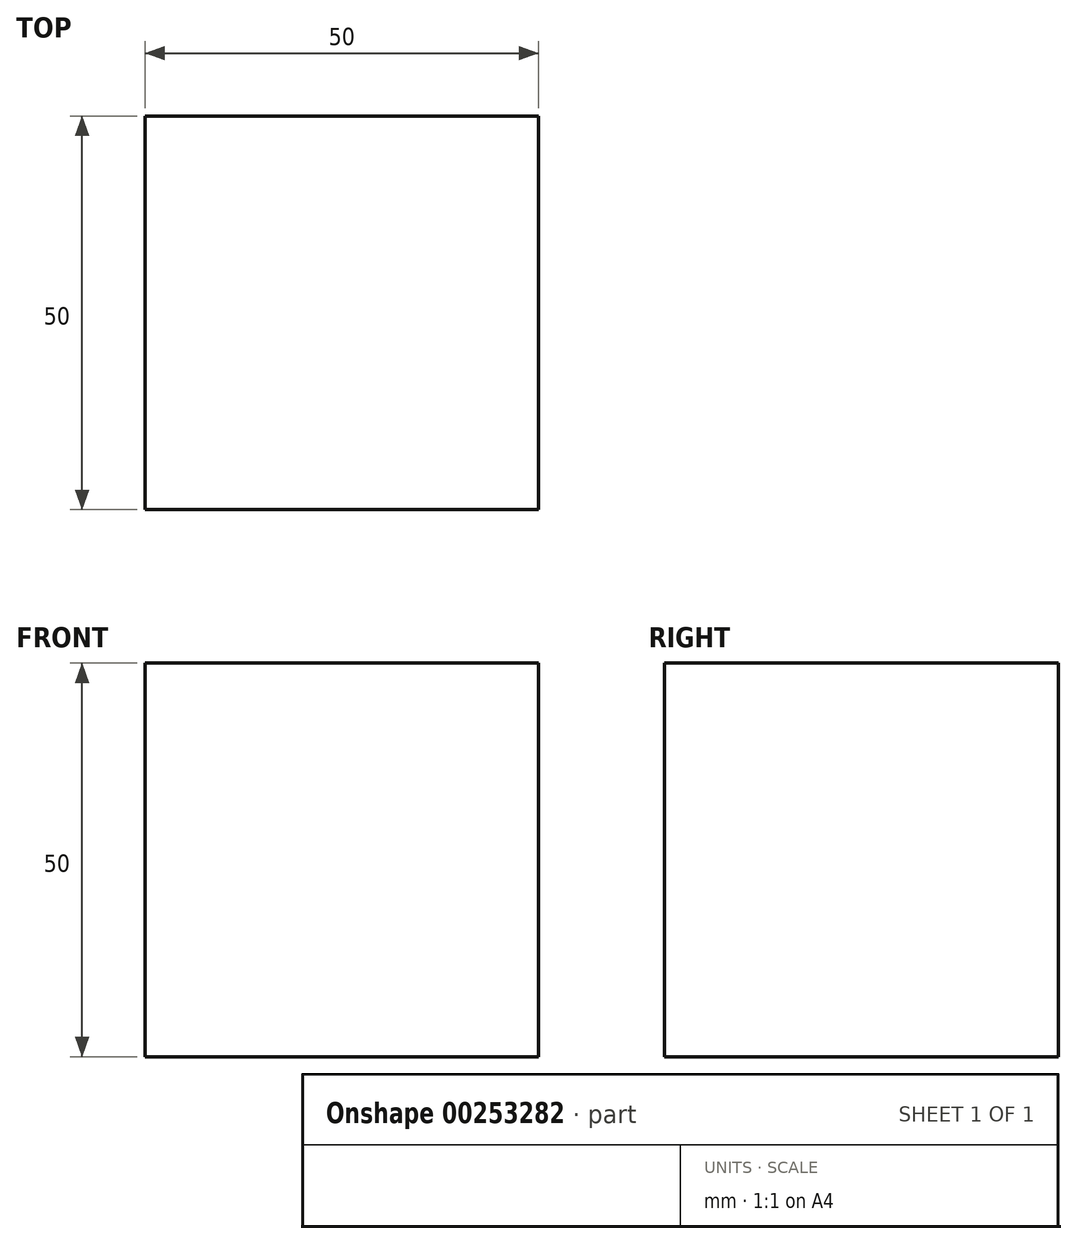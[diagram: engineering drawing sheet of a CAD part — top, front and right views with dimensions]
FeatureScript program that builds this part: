
annotation { "Feature Type Name" : "Feature", "Feature Type Description" : "" }
export const myFeature = defineFeature(function(context is Context, id is Id, definition is map)
    precondition{}
    {
        {
            var Q0;
            Q0=qCreatedBy(makeId("Front.planeOp"),FACE);
            var sketch = newSketch(context, id + "F0", { "sketchPlane" : qUnion([Q0])});
            skLineSegment(sketch, "E0.bottom", {"start": v(0, 0) * mm, "end": v(50, 0) * mm});
            skLineSegment(sketch, "E0.top", {"start": v(0, 50) * mm, "end": v(50, 50) * mm});
            skLineSegment(sketch, "E0.left", {"start": v(0, 0) * mm, "end": v(0, 50) * mm});
            skLineSegment(sketch, "E0.right", {"start": v(50, 0) * mm, "end": v(50, 50) * mm});
            skSolve(sketch);
        }
        {
            var Q0;
            Q0=makeQuery(id+"F0.imprint","IMPRINT",FACE,{"disambiguationData":[TD([[makeQuery(id+"F0.imprint","IMPRINT",EDGE,{"derivedFrom":sQuery(id+"F0.wireOp",EDGE,"E0.bottom")}),1.0]])]});
            extrude(context, id + "F1", {"entities" : qUnion([Q0]), "depth" : 50 * mm});
        }
    });
